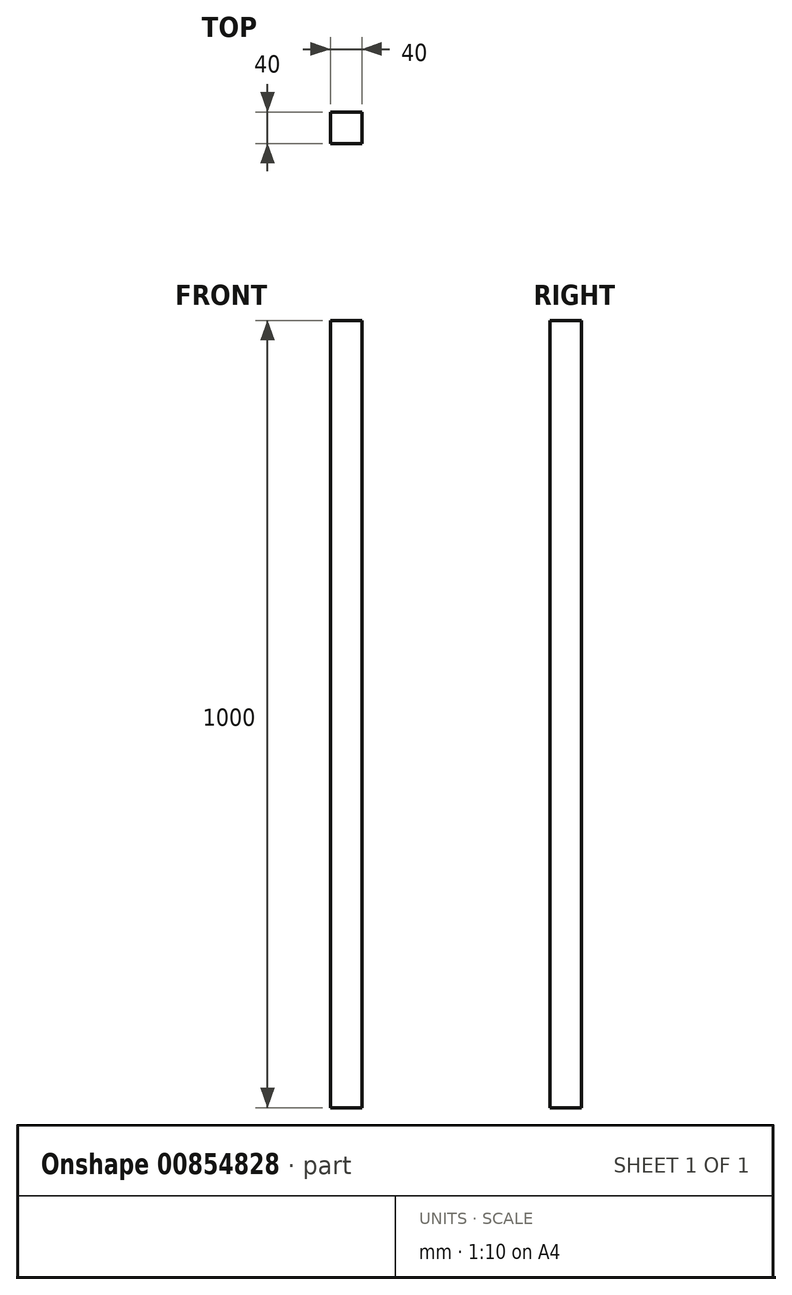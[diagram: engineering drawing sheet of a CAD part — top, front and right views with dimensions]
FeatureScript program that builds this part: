
annotation { "Feature Type Name" : "Feature", "Feature Type Description" : "" }
export const myFeature = defineFeature(function(context is Context, id is Id, definition is map)
    precondition{}
    {
        {
            var Q0;
            Q0=qCreatedBy(makeId("Top.planeOp"),FACE);
            var sketch = newSketch(context, id + "F0", { "sketchPlane" : qUnion([Q0])});
            skLineSegment(sketch, "E0.bottom", {"start": v(20, 20) * mm, "end": v(-20, 20) * mm});
            skLineSegment(sketch, "E0.top", {"start": v(20, -20) * mm, "end": v(-20, -20) * mm});
            skLineSegment(sketch, "E0.left", {"start": v(20, 20) * mm, "end": v(20, -20) * mm});
            skLineSegment(sketch, "E0.right", {"start": v(-20, 20) * mm, "end": v(-20, -20) * mm});
            skPoint(sketch, "E0.middle", {"position": v(0, 0) * mm});
            skSolve(sketch);
        }
        {
            var Q0;
            Q0=makeQuery(id+"F0.imprint","IMPRINT",FACE,{"disambiguationData":[TD([[makeQuery(id+"F0.imprint","IMPRINT",EDGE,{"derivedFrom":sQuery(id+"F0.wireOp",EDGE,"E0.bottom")}),1.0]])]});
            extrude(context, id + "F1", {"entities" : qUnion([Q0]), "depth" : 1000 * mm, "offsetDistance" : 25 * mm});
        }
    });
